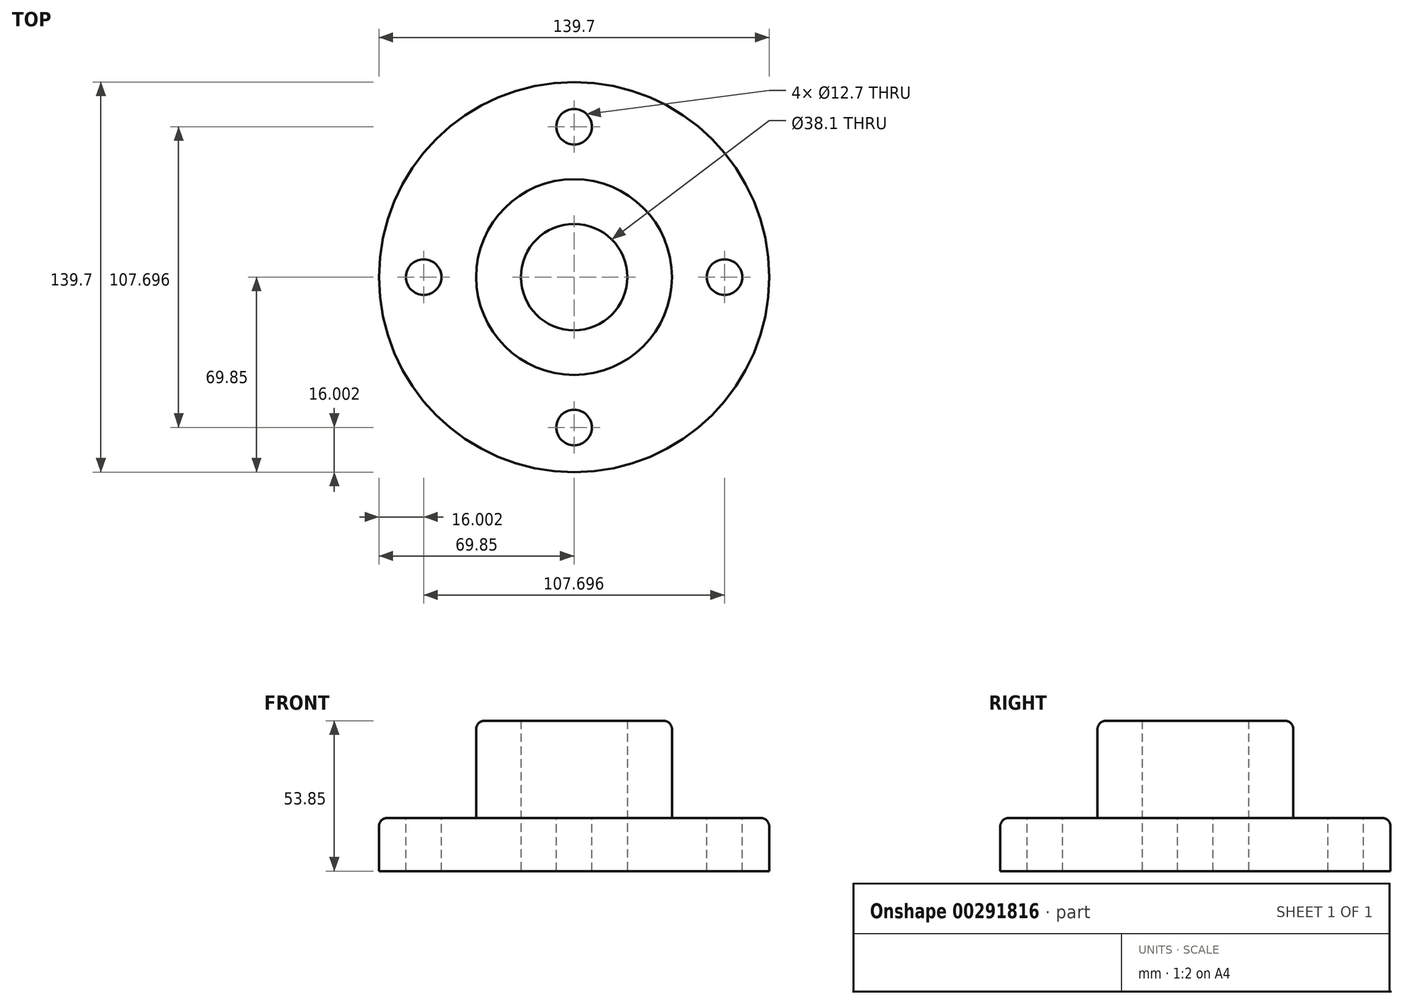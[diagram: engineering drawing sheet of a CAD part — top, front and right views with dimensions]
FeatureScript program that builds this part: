
annotation { "Feature Type Name" : "Feature", "Feature Type Description" : "" }
export const myFeature = defineFeature(function(context is Context, id is Id, definition is map)
    precondition{}
    {
        {
            var Q0;
            Q0=qCreatedBy(makeId("Front.planeOp"),FACE);
            var sketch = newSketch(context, id + "F0", { "sketchPlane" : qUnion([Q0])});
            skLineSegment(sketch, "E0", {"start": v(0, 0) * mm, "end": v(0, 78.71) * mm, "construction": true});
            skLineSegment(sketch, "E1.bottom", {"start": v(-19.05, 0) * mm, "end": v(-69.85, 0) * mm});
            skLineSegment(sketch, "E1.top", {"start": v(-19.05, 19.05) * mm, "end": v(-69.85, 19.05) * mm});
            skLineSegment(sketch, "E1.left", {"start": v(-19.05, 0) * mm, "end": v(-19.05, 19.05) * mm});
            skLineSegment(sketch, "E1.right", {"start": v(-69.85, 0) * mm, "end": v(-69.85, 19.05) * mm});
            skSolve(sketch);
        }
        {
            var Q0;
            Q0 = qSketchRegion(id + "F0", true);
            var Q1;
            Q1=sQuery(id+"F0.wireOp",EDGE,"E0");
            revolve(context, id + "F1", {"entities" : qUnion([Q0]), "axis" : qUnion([Q1]), "revolveType" : RevolveType.FULL});
        }
        {
            var Q0;
            Q0=qCreatedBy(makeId("Front.planeOp"),FACE);
            var sketch = newSketch(context, id + "F2", { "sketchPlane" : qUnion([Q0])});
            skLineSegment(sketch, "E2.bottom", {"start": v(-19.05, 19.05) * mm, "end": v(-35.05, 19.05) * mm});
            skLineSegment(sketch, "E2.top", {"start": v(-19.05, 53.85) * mm, "end": v(-35.05, 53.85) * mm});
            skLineSegment(sketch, "E2.left", {"start": v(-19.05, 19.05) * mm, "end": v(-19.05, 53.85) * mm});
            skLineSegment(sketch, "E2.right", {"start": v(-35.05, 19.05) * mm, "end": v(-35.05, 53.85) * mm});
            skSolve(sketch);
        }
        {
            var Q0;
            Q0 = qSketchRegion(id + "F2", true);
            var Q1;
            Q1=sQuery(id+"F0.wireOp",EDGE,"E0");
            revolve(context, id + "F3", {"operationType" : NewBodyOperationType.ADD, "entities" : qUnion([Q0]), "axis" : qUnion([Q1]), "revolveType" : RevolveType.FULL});
        }
        {
            var Q0;
            Q0=makeQuery(id+"F3.opRevolve","SWEPT_EDGE",EDGE,{"disambiguationData":[OSD([sQuery(id+"F2.wireOp",EDGE,"E2.top"),sQuery(id+"F2.wireOp",EDGE,"E2.right")])]});
            var Q1;
            Q1=makeQuery(id+"F1.opRevolve","SWEPT_EDGE",EDGE,{"disambiguationData":[OSD([sQuery(id+"F0.wireOp",EDGE,"E1.top"),sQuery(id+"F0.wireOp",EDGE,"E1.right")])]});
            var Q2;
            Q2=makeQuery(id+"F3.opRevolve","SWEPT_EDGE",EDGE,{"disambiguationData":[OSD([sQuery(id+"F2.wireOp",EDGE,"E2.bottom"),sQuery(id+"F2.wireOp",EDGE,"E2.right")])]});
            fillet(context, id + "F4", {"entities" : qUnion([Q0, Q1, Q2]), "radius" : 3.05 * mm, "tangentPropagation" : true, "allowEdgeOverflow" : false});
        }
        {
            var Q0;
            Q0=makeQuery(id+"F1.opRevolve","SWEPT_FACE",FACE,{"disambiguationData":[OSD([sQuery(id+"F0.wireOp",EDGE,"E1.top")])]});
            var sketch = newSketch(context, id + "F5", { "sketchPlane" : qUnion([Q0])});
            skCircle(sketch, "E3", {"center": v(0, 0) * mm, "radius": 53.85 * mm});
            skCircle(sketch, "E4", {"center": v(0, 53.85) * mm, "radius": 6.35 * mm});
            skCircle(sketch, "E5", {"center": v(53.85, 0) * mm, "radius": 6.35 * mm});
            skCircle(sketch, "E6", {"center": v(0, -53.85) * mm, "radius": 6.35 * mm});
            skCircle(sketch, "E7", {"center": v(-53.85, 0) * mm, "radius": 6.35 * mm});
            skSolve(sketch);
        }
        {
            var Q0;
            {var subQ0=sQuery(id+"F5.wireOp",EDGE,"E4");var subQ1=sQuery(id+"F5.wireOp",EDGE,"E3");var subQ2=makeQuery(id+"F5.imprint","INTERSECT",VERTEX,{"disambiguationData":[OD(0.0)],"derivedFrom":[subQ1,subQ0]});Q0=makeQuery(id+"F5.imprint","IMPRINT",FACE,{"disambiguationData":[TD([[makeQuery(id+"F5.imprint","IMPRINT",EDGE,{"disambiguationData":[TD([[subQ2,-1.0]])],"derivedFrom":subQ1}),1.0]])]});}
            var Q1;
            {var subQ0=sQuery(id+"F5.wireOp",EDGE,"E4");var subQ1=sQuery(id+"F5.wireOp",EDGE,"E3");var subQ2=makeQuery(id+"F5.imprint","INTERSECT",VERTEX,{"disambiguationData":[OD(0.0)],"derivedFrom":[subQ1,subQ0]});Q1=makeQuery(id+"F5.imprint","IMPRINT",FACE,{"disambiguationData":[TD([[makeQuery(id+"F5.imprint","IMPRINT",EDGE,{"disambiguationData":[TD([[subQ2,-1.0]])],"derivedFrom":subQ1}),-1.0]])]});}
            var Q2;
            {var subQ0=sQuery(id+"F5.wireOp",EDGE,"E7");var subQ1=sQuery(id+"F5.wireOp",EDGE,"E3");var subQ2=makeQuery(id+"F5.imprint","INTERSECT",VERTEX,{"disambiguationData":[OD(0.0)],"derivedFrom":[subQ1,subQ0]});Q2=makeQuery(id+"F5.imprint","IMPRINT",FACE,{"disambiguationData":[TD([[makeQuery(id+"F5.imprint","IMPRINT",EDGE,{"disambiguationData":[TD([[subQ2,-1.0]])],"derivedFrom":subQ1}),1.0]])]});}
            var Q3;
            {var subQ0=sQuery(id+"F5.wireOp",EDGE,"E7");var subQ1=sQuery(id+"F5.wireOp",EDGE,"E3");var subQ2=makeQuery(id+"F5.imprint","INTERSECT",VERTEX,{"disambiguationData":[OD(0.0)],"derivedFrom":[subQ1,subQ0]});Q3=makeQuery(id+"F5.imprint","IMPRINT",FACE,{"disambiguationData":[TD([[makeQuery(id+"F5.imprint","IMPRINT",EDGE,{"disambiguationData":[TD([[subQ2,-1.0]])],"derivedFrom":subQ1}),-1.0]])]});}
            var Q4;
            {var subQ0=sQuery(id+"F5.wireOp",EDGE,"E5");var subQ1=sQuery(id+"F5.wireOp",EDGE,"E3");var subQ2=makeQuery(id+"F5.imprint","INTERSECT",VERTEX,{"disambiguationData":[OD(0.0)],"derivedFrom":[subQ1,subQ0]});Q4=makeQuery(id+"F5.imprint","IMPRINT",FACE,{"disambiguationData":[TD([[makeQuery(id+"F5.imprint","IMPRINT",EDGE,{"disambiguationData":[TD([[subQ2,1.0]])],"derivedFrom":subQ1}),-1.0]])]});}
            var Q5;
            {var subQ0=sQuery(id+"F5.wireOp",EDGE,"E5");var subQ1=sQuery(id+"F5.wireOp",EDGE,"E3");var subQ2=makeQuery(id+"F5.imprint","INTERSECT",VERTEX,{"disambiguationData":[OD(0.0)],"derivedFrom":[subQ1,subQ0]});Q5=makeQuery(id+"F5.imprint","IMPRINT",FACE,{"disambiguationData":[TD([[makeQuery(id+"F5.imprint","IMPRINT",EDGE,{"disambiguationData":[TD([[subQ2,1.0]])],"derivedFrom":subQ1}),1.0]])]});}
            var Q6;
            {var subQ0=sQuery(id+"F5.wireOp",EDGE,"E6");var subQ1=sQuery(id+"F5.wireOp",EDGE,"E3");var subQ2=makeQuery(id+"F5.imprint","INTERSECT",VERTEX,{"disambiguationData":[OD(0.0)],"derivedFrom":[subQ1,subQ0]});Q6=makeQuery(id+"F5.imprint","IMPRINT",FACE,{"disambiguationData":[TD([[makeQuery(id+"F5.imprint","IMPRINT",EDGE,{"disambiguationData":[TD([[subQ2,-1.0]])],"derivedFrom":subQ1}),1.0]])]});}
            var Q7;
            {var subQ0=sQuery(id+"F5.wireOp",EDGE,"E6");var subQ1=sQuery(id+"F5.wireOp",EDGE,"E3");var subQ2=makeQuery(id+"F5.imprint","INTERSECT",VERTEX,{"disambiguationData":[OD(0.0)],"derivedFrom":[subQ1,subQ0]});Q7=makeQuery(id+"F5.imprint","IMPRINT",FACE,{"disambiguationData":[TD([[makeQuery(id+"F5.imprint","IMPRINT",EDGE,{"disambiguationData":[TD([[subQ2,-1.0]])],"derivedFrom":subQ1}),-1.0]])]});}
            extrude(context, id + "F6", {"entities" : qUnion([Q0, Q1, Q2, Q3, Q4, Q5, Q6, Q7]), "operationType" : NewBodyOperationType.REMOVE, "endBound" : BoundingType.THROUGH_ALL, "oppositeDirection" : true, "depth" : 25.4 * mm});
        }
    });
